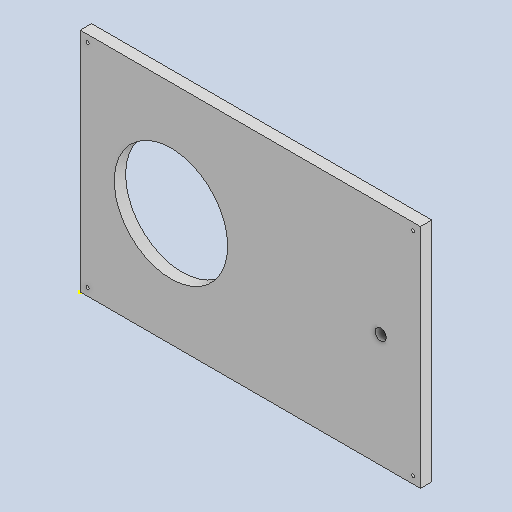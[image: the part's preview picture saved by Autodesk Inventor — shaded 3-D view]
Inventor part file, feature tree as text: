
AUTODESK INVENTOR PART (.ipt)
format: ipt  version: 2022 (Build 260153000, 153)  size: 137,216 bytes
history: native  units: mm
features: sketch x5, extrude x4
ambient origin geometry x8: Origin, YZ Plane, XZ Plane, XY Plane, X Axis, Y Axis, Z Axis, Center Point
bodies: Solid1 (feature_tree)
feature tree (9):
  extrude  "Extrusion1"  Depth=200.0mm
  extrude  "Extrusion2"  Depth=10.0mm
  sketch  "Sketch3"  dims[d5=100.0mm d6=80.0mm]
  extrude  "Extrusion3"  Depth=80.0mm
  extrude  "Extrusion4"  Depth=10.0mm
  sketch  "Sketch1"  dims[d0=300.0mm d1=200.0mm]
  sketch  "Sketch2"  dims[d2=10.0mm d3=0.0mm d4=100.0mm]
  sketch  "Sketch4"  dims[d7=0.0mm d8=0.0mm d9=10.0mm]
  sketch  "Sketch5"  dims[d10=100.0mm d11=30.0mm d12=10.0mm d13=0.0mm d14=2.903mm d16=2.903mm d17=2.903mm d18=5.0mm d19=5.0mm d20=2.903mm d21=5.0mm d22=5.0mm d23=5.0mm d24=5.0mm d25=5.0mm d26=5.0mm d27=0.0mm d28=0.0mm]
